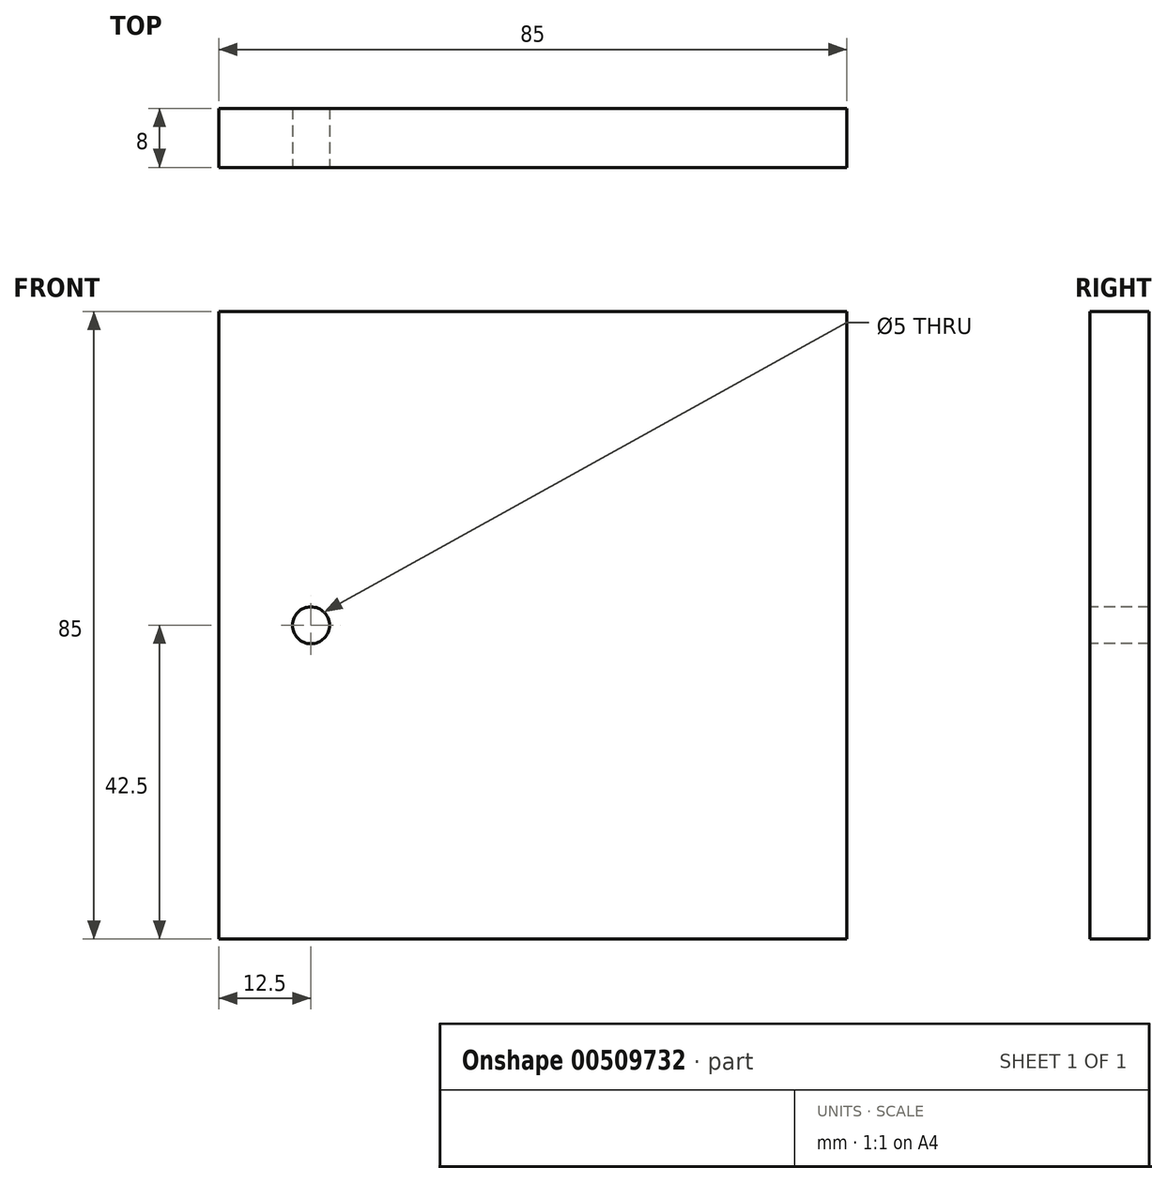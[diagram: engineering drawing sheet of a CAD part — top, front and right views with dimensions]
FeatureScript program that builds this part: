
annotation { "Feature Type Name" : "Feature", "Feature Type Description" : "" }
export const myFeature = defineFeature(function(context is Context, id is Id, definition is map)
    precondition{}
    {
        {
            var Q0;
            Q0=qCreatedBy(makeId("Front.planeOp"),FACE);
            var sketch = newSketch(context, id + "F0", { "sketchPlane" : qUnion([Q0])});
            skLineSegment(sketch, "E0.bottom", {"start": v(42.5, -42.5) * mm, "end": v(-42.5, -42.5) * mm});
            skLineSegment(sketch, "E0.top", {"start": v(42.5, 42.5) * mm, "end": v(-42.5, 42.5) * mm});
            skLineSegment(sketch, "E0.left", {"start": v(42.5, -42.5) * mm, "end": v(42.5, 42.5) * mm});
            skLineSegment(sketch, "E0.right", {"start": v(-42.5, -42.5) * mm, "end": v(-42.5, 42.5) * mm});
            skPoint(sketch, "E0.middle", {"position": v(0, 0) * mm});
            skCircle(sketch, "E1", {"center": v(30, 0) * mm, "radius": 4 * mm});
            skCircle(sketch, "E2.MirrorC", {"center": v(-30, 0) * mm, "radius": 4 * mm});
            skCircle(sketch, "E3", {"center": v(30, 0) * mm, "radius": 2.5 * mm});
            skCircle(sketch, "E4.MirrorC", {"center": v(-30, 0) * mm, "radius": 2.5 * mm});
            skSolve(sketch);
        }
        {
            var Q0;
            Q0=qCreatedBy(makeId("Front.planeOp"),FACE);
            cPlane(context, id + "F1", {"entities" : qUnion([Q0]), "cplaneType" : CPlaneType.OFFSET, "offset" : 2 * mm, "oppositeDirection" : true, "width" : 150 * mm, "height" : 150 * mm});
        }
        {
            var Q0;
            Q0=qCreatedBy(makeId("Front.planeOp"),FACE);
            cPlane(context, id + "F2", {"entities" : qUnion([Q0]), "cplaneType" : CPlaneType.OFFSET, "offset" : 8 * mm, "oppositeDirection" : true, "width" : 150 * mm, "height" : 150 * mm});
        }
        {
            var Q0;
            Q0=makeQuery(id+"F0.imprint","IMPRINT",FACE,{"disambiguationData":[TD([[makeQuery(id+"F0.imprint","IMPRINT",EDGE,{"derivedFrom":sQuery(id+"F0.wireOp",EDGE,"E0.bottom")}),-1.0]])]});
            var Q1;
            Q1=makeQuery(id+"F0.imprint","IMPRINT",FACE,{"disambiguationData":[TD([[makeQuery(id+"F0.imprint","IMPRINT",EDGE,{"derivedFrom":sQuery(id+"F0.wireOp",EDGE,"E1")}),1.0]])]});
            var Q2;
            Q2=makeQuery(id+"F0.imprint","IMPRINT",FACE,{"disambiguationData":[TD([[makeQuery(id+"F0.imprint","IMPRINT",EDGE,{"derivedFrom":sQuery(id+"F0.wireOp",EDGE,"E3")}),1.0]])]});
            var Q3;
            Q3=makeQuery(id+"F0.imprint","IMPRINT",FACE,{"disambiguationData":[TD([[makeQuery(id+"F0.imprint","IMPRINT",EDGE,{"derivedFrom":sQuery(id+"F0.wireOp",EDGE,"E2.MirrorC")}),-1.0]])]});
            var Q4;
            Q4=makeQuery(id+"F0.imprint","IMPRINT",FACE,{"disambiguationData":[TD([[makeQuery(id+"F0.imprint","IMPRINT",EDGE,{"derivedFrom":sQuery(id+"F0.wireOp",EDGE,"E4.MirrorC")}),-1.0]])]});
            extrude(context, id + "F3", {"entities" : qUnion([Q0, Q1, Q2, Q3, Q4]), "oppositeDirection" : true, "depth" : 8 * mm});
        }
    });
